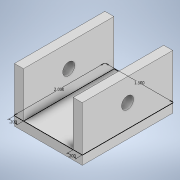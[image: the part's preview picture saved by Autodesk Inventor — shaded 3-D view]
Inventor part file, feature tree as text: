
AUTODESK INVENTOR PART (.ipt)
format: ipt  version: 2020 (Build 240168000, 168)  size: 113,664 bytes
history: native  units: in
note: dims shown in document units (in); Inventor stores cm internally (conversion verified against a paired STEP export)
features: sketch x2, extrude x2, hole x1
ambient origin geometry x8: Origin, YZ Plane, XZ Plane, XY Plane, X Axis, Y Axis, Z Axis, Center Point
bodies: Solid1 (feature_tree)
feature tree (5):
  sketch  "Sketch1"  dims[d0=1.5in d1=2.0in]
  extrude  "Extrusion1"  Depth=2.0in
  extrude  "Extrusion2"  Depth=0.2in
  hole  "Hole1"  [1 undecoded]
  sketch  "Sketch2"  dims[d2=0.2in d3=0.2in d4=1.0in d5=0.0in d6=0.2in d7=0.0in d8=0.5in d9=0.266in d10=0.75in d11=0.438in d12=0.25in d13=0.5635in d14=1.0in d15=0.8108in]
note: 1 required parameter value undecoded (feature->parameter linkage not recoverable at this tier; creation-order binding heuristic only, values carry confidence <= 0.55)
